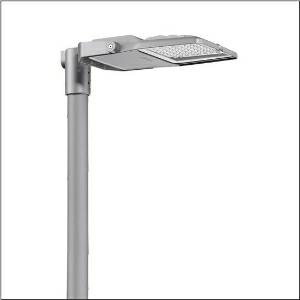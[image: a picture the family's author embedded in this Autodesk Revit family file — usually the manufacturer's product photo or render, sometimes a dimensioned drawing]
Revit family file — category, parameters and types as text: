
# Revit family: floodlight_fl_21_iq_mini___pl33t_5xa7771c4f3a_1d16
name_source: partatom
category: Lighting Fixtures
units: mm (PartAtom-declared; Revit-internal decimal feet)

## family parameters
Cut with Voids When Loaded = No
Host = Face
Light Source = No
Part Type = Normal
Room Calculation Point = No
Round Connector Dimension = Use Diameter
Shared = No

## types (1)
- --- (1 x LED, 12570 lm, 87.2 W, 4000K)
    Apparent Load = 87 VA
    CIE Flux Codes = 26 75 99 100 100
    Color Rendering = 70
    Color Temperature = 4000K
    Default Elevation = 1800 mm
    Description = Floodlight FL 21 iQ mini, floodlight, primary light control with lens, of PMMA, primary optical cover: protective disc, of toughened safety glass, transparent, light distribution: PL33T, light emission: direct distribution, installation type: surface-mounted, LED, High Power LED, rated luminous flux: 12.570lm, luminous efficacy: 144lm/W, light colour: 740, colour temperature: 4000K, control gear: iQ Comfort/DALI, control: Auto-Match, Temp-Guard, Lumen-Switch, Night-Set, Smart-Wire, Light-Fading, Desk-Remote (wireless, voltage-free reading and setting of iQ features in the workshop via application-optimized NFC function/RFID function), optimised constant luminous flux control (CLO 2.0), with terminal, 6-pole, mains connection: 220..240V, AC, 50/60Hz, start of lifetime: 87W, end of service life: 92W, reduction: 40W, luminaire housing, of diecast aluminium, powder-coated, Siteco® metallic grey (DB 702S), corrosivity category C5 mid according to DIN EN ISO 12944, suitable for swimming pools, chlorine-resistant, sealing non-destructively replaceable, please order mast flange separately, mast bracket, of steel, galvanised, powder-coated, Siteco® metallic grey (DB 702S), protection rating (complete): IP66, insulation class (complete): insulation class II (safety insulation), certification: CE, ENEC, VDE, protection symbol: D, impact resistance: IK08, permissible operating ambient temperature: -40..+40°C, permissible operating ambient temperature for outdoor applications: -40..+50°C, standard: DIN EN 12944, LABS conformity tested according to VDMA 24364:2018-05, packaging unit: 1 piece

Light Distribution: PL33T
    Height = 70 mm
    Lamp = 1 x LED
    Lamp Light Flux = 12570 lm
    Lamp Power = 87.2 W
    Lamp count = 1
    Length = 485 mm
    Luminous efficacy = 144 lm/W
    Manufacturer = Siteco
    ModVariant = No
    Model = 5XA7771C4F3A
    Number of Poles = 1
    OnlyDefault = Yes
    Power Factor = 1
    Product Name = Floodlight FL 21 iQ mini | PL33T
    Product group = floodlight | pylon annexe
    ProductGroupID = 6201
    Protection Class = Protection class II
    Protection Degree = IP 66
    RLX_Detail_Level = 1
    RLX_Emergency_Light_Flux = 0 lm
    RLX_Emergency_Type = 0
    RLX_Emergency_Type_DB = No
    RlxData = <blob elided: 101233 chars, md5=ef4e85ba>
    Socket = socket
    Standby Power = 0 W
    System Light Flux = 12570 lm
    System Power = 87 W
    Type Comments = factory setting: luminous flux: 100 % | dim-lin: 254 | 456 mA
    Type Image = l_1007125.jpg
    URL = http://relux.com
    VarID = @adj_171077
    Voltage = 0 V
    Weight = 0.00 kg
    Width = 337 mm

## geometry (parser evidence)
native form markers: Blend x4, Sweep x13
no freeform markers — native parametric forms only
